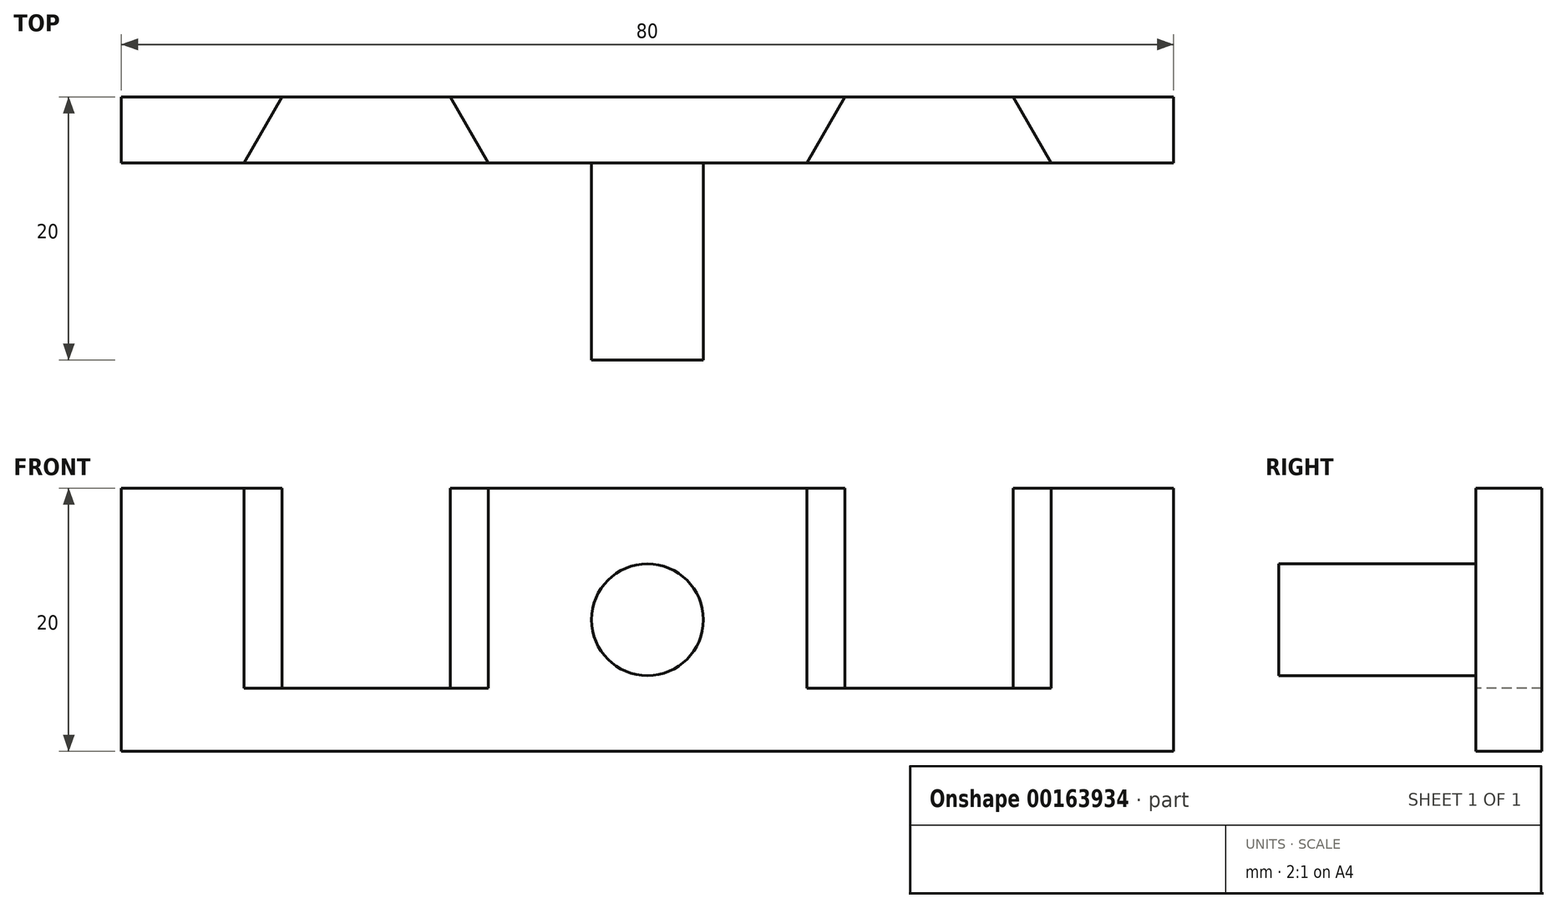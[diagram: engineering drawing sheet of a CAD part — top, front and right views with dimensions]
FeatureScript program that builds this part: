
annotation { "Feature Type Name" : "Feature", "Feature Type Description" : "" }
export const myFeature = defineFeature(function(context is Context, id is Id, definition is map)
    precondition{}
    {
        {
            var Q0;
            Q0=qCreatedBy(makeId("Top.planeOp"),FACE);
            var sketch = newSketch(context, id + "F0", { "sketchPlane" : qUnion([Q0])});
            skLineSegment(sketch, "E0", {"start": v(0, 0) * mm, "end": v(-40, 0) * mm});
            skLineSegment(sketch, "E1", {"start": v(-40, 0) * mm, "end": v(-40, 20) * mm});
            skLineSegment(sketch, "E2", {"start": v(-40, 20) * mm, "end": v(-27.8, 20) * mm});
            skLineSegment(sketch, "E3", {"start": v(-27.8, 20) * mm, "end": v(-32.8, 11.34) * mm});
            skLineSegment(sketch, "E4", {"start": v(-32.8, 11.34) * mm, "end": v(-10, 11.34) * mm});
            skLineSegment(sketch, "E5", {"start": v(-10, 11.34) * mm, "end": v(-15, 20) * mm});
            skLineSegment(sketch, "E6", {"start": v(-15, 20) * mm, "end": v(0, 20) * mm});
            skLineSegment(sketch, "E7", {"start": v(0, 20) * mm, "end": v(0, 0) * mm});
            skLineSegment(sketch, "E8.MirrorCS", {"start": v(15, 20) * mm, "end": v(0, 20) * mm});
            skLineSegment(sketch, "E9.MirrorCS", {"start": v(10, 11.34) * mm, "end": v(15, 20) * mm});
            skLineSegment(sketch, "E10.MirrorCS", {"start": v(0, 0) * mm, "end": v(40, 0) * mm});
            skLineSegment(sketch, "E11.MirrorCS", {"start": v(32.8, 11.34) * mm, "end": v(10, 11.34) * mm});
            skLineSegment(sketch, "E12.MirrorCS", {"start": v(27.8, 20) * mm, "end": v(32.8, 11.34) * mm});
            skLineSegment(sketch, "E13.MirrorCS", {"start": v(40, 20) * mm, "end": v(27.8, 20) * mm});
            skLineSegment(sketch, "E14.MirrorCS", {"start": v(40, 0) * mm, "end": v(40, 20) * mm});
            skLineSegment(sketch, "E15", {"start": v(-27.8, 20) * mm, "end": v(-15, 20) * mm});
            skLineSegment(sketch, "E16", {"start": v(15, 20) * mm, "end": v(27.8, 20) * mm});
            skSolve(sketch);
        }
        {
            var Q0;
            Q0 = qSketchRegion(id + "F0", true);
            extrude(context, id + "F1", {"entities" : qUnion([Q0]), "oppositeDirection" : true, "depth" : 20 * mm});
        }
        {
            var Q0;
            Q0=makeQuery(id+"F0.imprint","IMPRINT",FACE,{"disambiguationData":[TD([[makeQuery(id+"F0.imprint","IMPRINT",EDGE,{"derivedFrom":sQuery(id+"F0.wireOp",EDGE,"E3")}),1.0]])]});
            var Q1;
            Q1=makeQuery(id+"F0.imprint","IMPRINT",FACE,{"disambiguationData":[TD([[makeQuery(id+"F0.imprint","IMPRINT",EDGE,{"derivedFrom":sQuery(id+"F0.wireOp",EDGE,"E9.MirrorCS")}),-1.0]])]});
            extrude(context, id + "F2", {"entities" : qUnion([Q0, Q1]), "operationType" : NewBodyOperationType.REMOVE, "oppositeDirection" : true, "depth" : 15.2 * mm});
        }
        {
            var Q0;
            Q0=makeQuery(id+"F1.opExtrude","SWEPT_FACE",FACE,{"disambiguationData":[OSD([sQuery(id+"F0.wireOp",EDGE,"E0"),sQuery(id+"F0.wireOp",EDGE,"E10.MirrorCS")])]});
            var sketch = newSketch(context, id + "F3", { "sketchPlane" : qUnion([Q0])});
            skLineSegment(sketch, "E17", {"start": v(0, 0) * mm, "end": v(0, -20) * mm});
            skLineSegment(sketch, "E18", {"start": v(0, -20) * mm, "end": v(0, -10) * mm});
            skLineSegment(sketch, "E19", {"start": v(0, -10) * mm, "end": v(-3.74, -10) * mm});
            skCircle(sketch, "E20", {"center": v(0, -10) * mm, "radius": 4.25 * mm});
            skSolve(sketch);
        }
        {
            var Q0;
            {var subQ0=sQuery(id+"F3.wireOp",EDGE,"E18");var subQ1=sQuery(id+"F3.wireOp",EDGE,"E17");var subQ2=makeQuery(id+"F3.imprint","INTERSECT",VERTEX,{"derivedFrom":[subQ1,subQ0]});Q0=makeQuery(id+"F3.imprint","IMPRINT",FACE,{"disambiguationData":[TD([[makeQuery(id+"F3.imprint","IMPRINT",EDGE,{"disambiguationData":[TD([[subQ2,1.0]])],"derivedFrom":subQ1}),1.0]])]});}
            var Q1;
            {var subQ0=sQuery(id+"F3.wireOp",EDGE,"E18");var subQ1=sQuery(id+"F3.wireOp",EDGE,"E17");var subQ2=makeQuery(id+"F3.imprint","INTERSECT",VERTEX,{"derivedFrom":[subQ1,subQ0]});Q1=makeQuery(id+"F3.imprint","IMPRINT",FACE,{"disambiguationData":[TD([[makeQuery(id+"F3.imprint","IMPRINT",EDGE,{"disambiguationData":[TD([[subQ2,1.0]])],"derivedFrom":subQ1}),-1.0]])]});}
            extrude(context, id + "F4", {"entities" : qUnion([Q0, Q1]), "operationType" : NewBodyOperationType.REMOVE, "oppositeDirection" : true, "depth" : 15 * mm});
        }
    });
